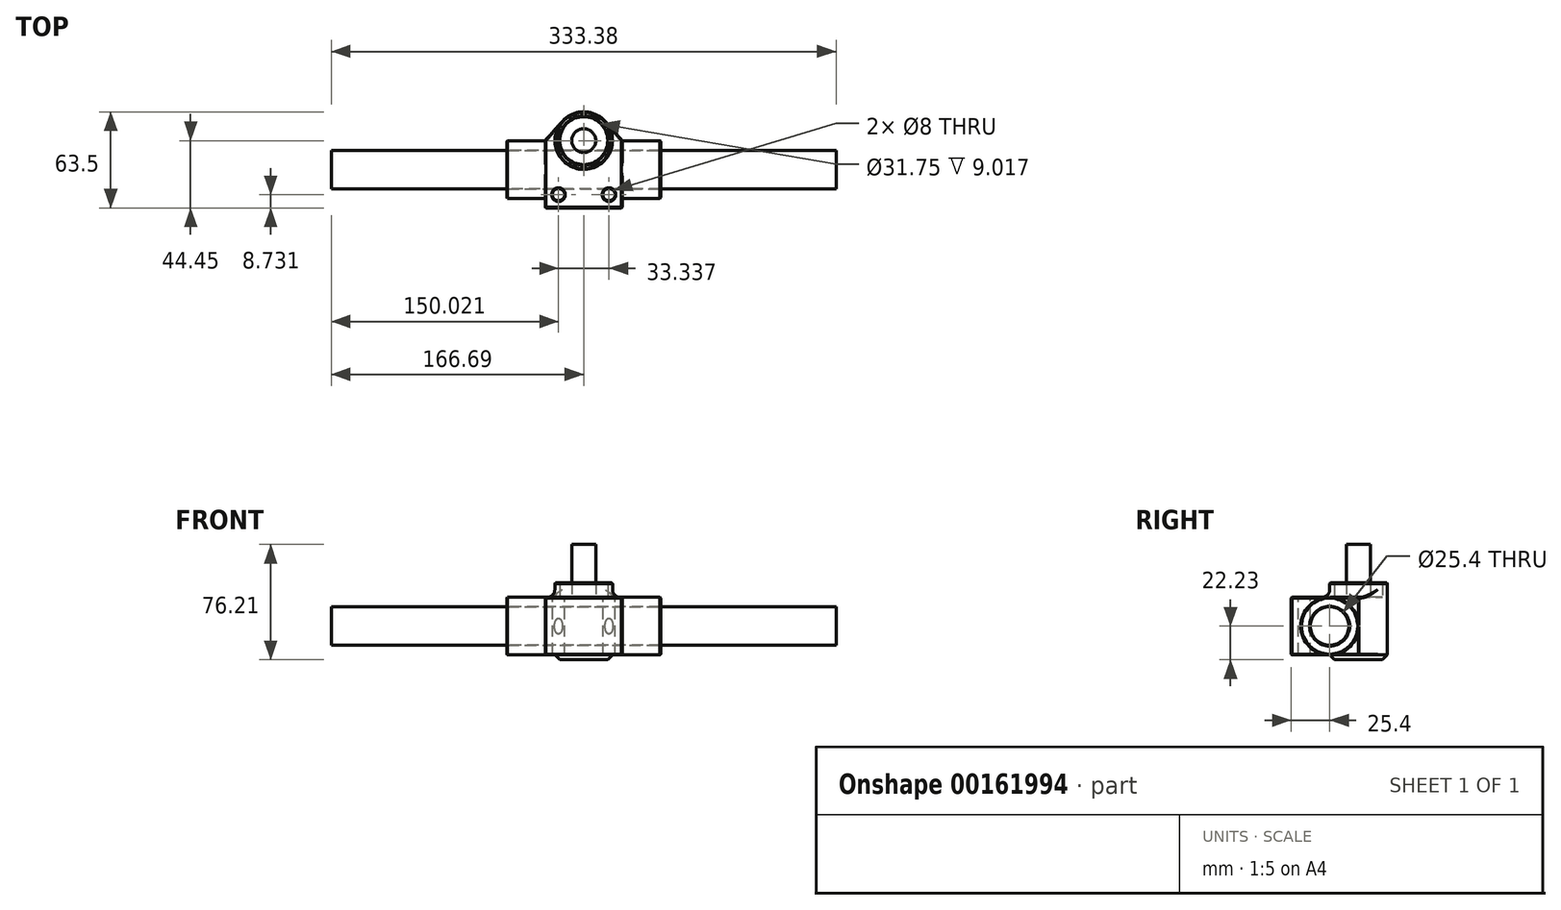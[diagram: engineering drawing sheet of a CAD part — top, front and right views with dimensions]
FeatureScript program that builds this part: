
annotation { "Feature Type Name" : "Feature", "Feature Type Description" : "" }
export const myFeature = defineFeature(function(context is Context, id is Id, definition is map)
    precondition{}
    {
        {
            var Q0;
            Q0=qCreatedBy(makeId("Top.planeOp"),FACE);
            var sketch = newSketch(context, id + "F0", { "sketchPlane" : qUnion([Q0])});
            skArc(sketch, "E0", {"start": v(-14.29, 12.6) * mm, "mid": v(0, 19.05) * mm, "end": v(14.29, 12.6) * mm});
            skLineSegment(sketch, "E1", {"start": v(-14.29, 12.6) * mm, "end": v(-25.4, 0) * mm});
            skLineSegment(sketch, "E2", {"start": v(14.29, 12.6) * mm, "end": v(25.4, 0) * mm});
            skLineSegment(sketch, "E3", {"start": v(25.4, 0) * mm, "end": v(25.4, -44.45) * mm});
            skLineSegment(sketch, "E4", {"start": v(25.4, -44.45) * mm, "end": v(-25.4, -44.45) * mm});
            skLineSegment(sketch, "E5", {"start": v(-25.4, -44.45) * mm, "end": v(-25.4, 0) * mm});
            skSolve(sketch);
        }
        {
            var Q0;
            Q0 = qSketchRegion(id + "F0", true);
            extrude(context, id + "F1", {"entities" : qUnion([Q0]), "endBound" : BoundingType.SYMMETRIC, "depth" : 38.1 * mm});
        }
        {
            var Q0;
            Q0=qCreatedBy(makeId("Right.planeOp"),FACE);
            var sketch = newSketch(context, id + "F2", { "sketchPlane" : qUnion([Q0])});
            skCircle(sketch, "E6", {"center": v(-19.05, 0) * mm, "radius": 19.05 * mm});
            skSolve(sketch);
        }
        {
            var Q0;
            Q0 = qSketchRegion(id + "F2", true);
            extrude(context, id + "F3", {"entities" : qUnion([Q0]), "operationType" : NewBodyOperationType.ADD, "endBound" : BoundingType.SYMMETRIC, "depth" : 101.6 * mm});
        }
        {
            var Q0;
            Q0=qCreatedBy(makeId("Right.planeOp"),FACE);
            var sketch = newSketch(context, id + "F4", { "sketchPlane" : qUnion([Q0])});
            skCircle(sketch, "E7", {"center": v(-19.05, 0) * mm, "radius": 12.7 * mm});
            skSolve(sketch);
        }
        {
            var Q0;
            Q0 = qSketchRegion(id + "F4", true);
            extrude(context, id + "F5", {"entities" : qUnion([Q0]), "operationType" : NewBodyOperationType.REMOVE, "endBound" : BoundingType.THROUGH_ALL, "oppositeDirection" : true, "depth" : 25.4 * mm, "hasSecondDirection" : true, "secondDirectionBound" : SecondDirectionBoundingType.THROUGH_ALL, "secondDirectionOppositeDirection" : false, "secondDirectionDepth" : 25.4 * mm});
        }
        {
            var Q0;
            Q0=makeQuery(id+"F1.opExtrude","CAP_FACE",FACE,{"disambiguationData":[OSD([sQuery(id+"F0.wireOp",EDGE,"E0"),sQuery(id+"F0.wireOp",EDGE,"E1"),sQuery(id+"F0.wireOp",EDGE,"E2"),sQuery(id+"F0.wireOp",EDGE,"E3"),sQuery(id+"F0.wireOp",EDGE,"E4"),sQuery(id+"F0.wireOp",EDGE,"E5")])],"isStart":false});
            var sketch = newSketch(context, id + "F6", { "sketchPlane" : qUnion([Q0])});
            skCircle(sketch, "E8", {"center": v(0, 0) * mm, "radius": 19.05 * mm});
            skCircle(sketch, "E9.0", {"center": v(0, 0) * mm, "radius": 15.88 * mm});
            skSolve(sketch);
        }
        {
            var Q0;
            Q0 = qSketchRegion(id + "F6", true);
            extrude(context, id + "F7", {"entities" : qUnion([Q0]), "operationType" : NewBodyOperationType.ADD, "depth" : 9.52 * mm});
        }
        {
            var Q0;
            Q0=makeQuery(id+"F7.boolean.opBoolean","SPLIT",FACE,{"disambiguationData":[TD([makeQuery(id+"F7.opExtrude","SWEPT_FACE",FACE,{"disambiguationData":[OSD([sQuery(id+"F6.wireOp",EDGE,"E9.0")])]})])],"derivedFrom":makeQuery(id+"F1.opExtrude","CAP_FACE",FACE,{"disambiguationData":[OSD([sQuery(id+"F0.wireOp",EDGE,"E0"),sQuery(id+"F0.wireOp",EDGE,"E1"),sQuery(id+"F0.wireOp",EDGE,"E2"),sQuery(id+"F0.wireOp",EDGE,"E3"),sQuery(id+"F0.wireOp",EDGE,"E4"),sQuery(id+"F0.wireOp",EDGE,"E5")])],"isStart":false})});
            var sketch = newSketch(context, id + "F8", { "sketchPlane" : qUnion([Q0])});
            skCircle(sketch, "E10", {"center": v(0, 0) * mm, "radius": 7.94 * mm});
            skSolve(sketch);
        }
        {
            var Q0;
            Q0=makeQuery(id+"F8.imprint","IMPRINT",FACE,{"disambiguationData":[TD([[makeQuery(id+"F8.imprint","IMPRINT",EDGE,{"derivedFrom":sQuery(id+"F8.wireOp",EDGE,"E10")}),1.0]])]});
            extrude(context, id + "F9", {"entities" : qUnion([Q0]), "depth" : 34.92 * mm});
        }
        {
            var Q0;
            Q0=makeQuery(id+"F1.opExtrude","CAP_FACE",FACE,{"disambiguationData":[OSD([sQuery(id+"F0.wireOp",EDGE,"E0"),sQuery(id+"F0.wireOp",EDGE,"E1"),sQuery(id+"F0.wireOp",EDGE,"E2"),sQuery(id+"F0.wireOp",EDGE,"E3"),sQuery(id+"F0.wireOp",EDGE,"E4"),sQuery(id+"F0.wireOp",EDGE,"E5")])],"isStart":true});
            var sketch = newSketch(context, id + "F10", { "sketchPlane" : qUnion([Q0])});
            skCircle(sketch, "E11", {"center": v(0, 0) * mm, "radius": 19.05 * mm});
            skSolve(sketch);
        }
        {
            var Q0;
            Q0 = qSketchRegion(id + "F10", true);
            extrude(context, id + "F11", {"entities" : qUnion([Q0]), "operationType" : NewBodyOperationType.ADD, "depth" : 3.17 * mm});
        }
        {
            var Q0;
            {var subQ0=sQuery(id+"F0.wireOp",EDGE,"E3");var subQ1=sQuery(id+"F0.wireOp",EDGE,"E2");var subQ2=sQuery(id+"F0.wireOp",EDGE,"E1");var subQ3=sQuery(id+"F0.wireOp",EDGE,"E0");var subQ4=sQuery(id+"F0.wireOp",EDGE,"E4");var subQ5=sQuery(id+"F0.wireOp",EDGE,"E5");Q0=makeQuery(id+"F7.boolean.opBoolean","SPLIT",FACE,{"disambiguationData":[TD([makeQuery(id+"F1.opExtrude","SWEPT_FACE",FACE,{"disambiguationData":[OSD([subQ3])]})])],"derivedFrom":makeQuery(id+"F1.opExtrude","CAP_FACE",FACE,{"disambiguationData":[OSD([subQ3,subQ2,subQ1,subQ0,subQ4,subQ5])],"isStart":false})});}
            var sketch = newSketch(context, id + "F12", { "sketchPlane" : qUnion([Q0])});
            skLineSegment(sketch, "E12", {"start": v(-16.67, -35.72) * mm, "end": v(16.67, -35.72) * mm, "construction": true});
            skPoint(sketch, "E13", {"position": v(0, -35.72) * mm});
            skCircle(sketch, "E14", {"center": v(-16.67, -35.72) * mm, "radius": 4 * mm});
            skCircle(sketch, "E15", {"center": v(16.67, -35.72) * mm, "radius": 4 * mm});
            skSolve(sketch);
        }
        {
            var Q0;
            Q0 = qSketchRegion(id + "F12", true);
            extrude(context, id + "F13", {"entities" : qUnion([Q0]), "operationType" : NewBodyOperationType.REMOVE, "endBound" : BoundingType.THROUGH_ALL, "oppositeDirection" : true, "depth" : 25.4 * mm});
        }
        {
            var Q0;
            Q0=makeQuery(id+"F11.opExtrude","CAP_EDGE",EDGE,{"disambiguationData":[OSD([sQuery(id+"F10.wireOp",EDGE,"E11")])],"isStart":false});
            chamfer(context, id + "F14", {"entities" : qUnion([Q0]), "width" : 3.17 * mm, "tangentPropagation" : true});
        }
        {
            var Q0;
            Q0=makeQuery(id+"F7.opExtrude","CAP_EDGE",EDGE,{"disambiguationData":[OSD([sQuery(id+"F6.wireOp",EDGE,"E8")])],"isStart":true});
            fillet(context, id + "F15", {"entities" : qUnion([Q0]), "radius" : 5.08 * mm, "tangentPropagation" : true, "allowEdgeOverflow" : false});
        }
        {
            var Q0;
            Q0=makeQuery(id+"F13.boolean.opBoolean","COPY",FACE,{"derivedFrom":makeQuery(id+"F13.opExtrude","SWEPT_FACE",FACE,{"disambiguationData":[OSD([sQuery(id+"F12.wireOp",EDGE,"E15")])]})});
            var Q1;
            Q1=makeQuery(id+"F13.boolean.opBoolean","COPY",FACE,{"derivedFrom":makeQuery(id+"F13.opExtrude","SWEPT_FACE",FACE,{"disambiguationData":[OSD([sQuery(id+"F12.wireOp",EDGE,"E14")])]})});
            var Q2;
            Q2=makeQuery(id+"F3.opExtrude","CAP_FACE",FACE,{"disambiguationData":[OSD([sQuery(id+"F2.wireOp",EDGE,"E6")])],"isStart":false});
            var Q3;
            Q3=makeQuery(id+"F7.opExtrude","CAP_FACE",FACE,{"disambiguationData":[OSD([sQuery(id+"F6.wireOp",EDGE,"E8"),sQuery(id+"F6.wireOp",EDGE,"E9.0")])],"isStart":false});
            var Q4;
            Q4=makeQuery(id+"F3.opExtrude","CAP_FACE",FACE,{"disambiguationData":[OSD([sQuery(id+"F2.wireOp",EDGE,"E6")])],"isStart":true});
            var Q5;
            {var subQ0=sQuery(id+"F0.wireOp",EDGE,"E3");var subQ1=sQuery(id+"F0.wireOp",EDGE,"E2");Q5=makeQuery(id+"F3.boolean.opBoolean","SPLIT",EDGE,{"disambiguationData":[TD([makeQuery(id+"F1.opExtrude","SWEPT_FACE",FACE,{"disambiguationData":[OSD([subQ1])]})])],"derivedFrom":makeQuery(id+"F1.opExtrude","CAP_EDGE",EDGE,{"disambiguationData":[OSD([subQ0])],"isStart":false})});}
            var Q6;
            Q6=makeQuery(id+"F1.opExtrude","CAP_EDGE",EDGE,{"disambiguationData":[OSD([sQuery(id+"F0.wireOp",EDGE,"E4")])],"isStart":false});
            var Q7;
            {var subQ0=sQuery(id+"F0.wireOp",EDGE,"E5");var subQ1=sQuery(id+"F0.wireOp",EDGE,"E4");Q7=makeQuery(id+"F3.boolean.opBoolean","SPLIT",EDGE,{"disambiguationData":[TD([makeQuery(id+"F1.opExtrude","SWEPT_FACE",FACE,{"disambiguationData":[OSD([subQ1])]})])],"derivedFrom":makeQuery(id+"F1.opExtrude","CAP_EDGE",EDGE,{"disambiguationData":[OSD([subQ0])],"isStart":false})});}
            var Q8;
            Q8=makeQuery(id+"F1.opExtrude","SWEPT_EDGE",EDGE,{"disambiguationData":[OSD([sQuery(id+"F0.wireOp",EDGE,"E4"),sQuery(id+"F0.wireOp",EDGE,"E5")])]});
            var Q9;
            Q9=makeQuery(id+"F1.opExtrude","SWEPT_EDGE",EDGE,{"disambiguationData":[OSD([sQuery(id+"F0.wireOp",EDGE,"E3"),sQuery(id+"F0.wireOp",EDGE,"E4")])]});
            var Q10;
            Q10=makeQuery(id+"F1.opExtrude","CAP_EDGE",EDGE,{"disambiguationData":[OSD([sQuery(id+"F0.wireOp",EDGE,"E4")])],"isStart":true});
            var Q11;
            {var subQ0=sQuery(id+"F0.wireOp",EDGE,"E4");var subQ1=sQuery(id+"F0.wireOp",EDGE,"E3");Q11=makeQuery(id+"F3.boolean.opBoolean","SPLIT",EDGE,{"disambiguationData":[TD([makeQuery(id+"F1.opExtrude","SWEPT_FACE",FACE,{"disambiguationData":[OSD([subQ0])]})])],"derivedFrom":makeQuery(id+"F1.opExtrude","CAP_EDGE",EDGE,{"disambiguationData":[OSD([subQ1])],"isStart":true})});}
            var Q12;
            {var subQ0=sQuery(id+"F0.wireOp",EDGE,"E5");var subQ1=sQuery(id+"F0.wireOp",EDGE,"E4");Q12=makeQuery(id+"F3.boolean.opBoolean","SPLIT",EDGE,{"disambiguationData":[TD([makeQuery(id+"F1.opExtrude","SWEPT_FACE",FACE,{"disambiguationData":[OSD([subQ1])]})])],"derivedFrom":makeQuery(id+"F1.opExtrude","CAP_EDGE",EDGE,{"disambiguationData":[OSD([subQ0])],"isStart":true})});}
            var Q13;
            Q13=makeQuery(id+"F1.opExtrude","CAP_EDGE",EDGE,{"disambiguationData":[OSD([sQuery(id+"F0.wireOp",EDGE,"E1")])],"isStart":true});
            var Q14;
            Q14=makeQuery(id+"F1.opExtrude","CAP_EDGE",EDGE,{"disambiguationData":[OSD([sQuery(id+"F0.wireOp",EDGE,"E2")])],"isStart":true});
            var Q15;
            {var subQ0=sQuery(id+"F0.wireOp",EDGE,"E5");var subQ1=sQuery(id+"F0.wireOp",EDGE,"E1");Q15=makeQuery(id+"F3.boolean.opBoolean","SPLIT",EDGE,{"disambiguationData":[TD([makeQuery(id+"F1.opExtrude","CAP_FACE",FACE,{"disambiguationData":[OSD([sQuery(id+"F0.wireOp",EDGE,"E0"),subQ1,sQuery(id+"F0.wireOp",EDGE,"E2"),sQuery(id+"F0.wireOp",EDGE,"E3"),sQuery(id+"F0.wireOp",EDGE,"E4"),subQ0])],"isStart":false})])],"derivedFrom":makeQuery(id+"F1.opExtrude","SWEPT_EDGE",EDGE,{"disambiguationData":[OSD([subQ1,subQ0])]})});}
            var Q16;
            {var subQ0=sQuery(id+"F0.wireOp",EDGE,"E3");var subQ1=sQuery(id+"F0.wireOp",EDGE,"E2");Q16=makeQuery(id+"F3.boolean.opBoolean","SPLIT",EDGE,{"disambiguationData":[TD([makeQuery(id+"F1.opExtrude","CAP_FACE",FACE,{"disambiguationData":[OSD([sQuery(id+"F0.wireOp",EDGE,"E0"),sQuery(id+"F0.wireOp",EDGE,"E1"),subQ1,subQ0,sQuery(id+"F0.wireOp",EDGE,"E4"),sQuery(id+"F0.wireOp",EDGE,"E5")])],"isStart":true})])],"derivedFrom":makeQuery(id+"F1.opExtrude","SWEPT_EDGE",EDGE,{"disambiguationData":[OSD([subQ1,subQ0])]})});}
            var Q17;
            Q17=makeQuery(id+"F15.opFillet","BLEND_EDGE",EDGE,{"blendedFrom":[makeQuery(id+"F7.opExtrude","CAP_EDGE",EDGE,{"disambiguationData":[OSD([sQuery(id+"F6.wireOp",EDGE,"E8")])],"isStart":true}),makeQuery(id+"F1.opExtrude","SWEPT_FACE",FACE,{"disambiguationData":[OSD([sQuery(id+"F0.wireOp",EDGE,"E2")])]})],"blendedInto":[makeQuery(id+"F1.opExtrude","SWEPT_FACE",FACE,{"disambiguationData":[OSD([sQuery(id+"F0.wireOp",EDGE,"E2")])]})]});
            var Q18;
            Q18=makeQuery(id+"F15.opFillet","BLEND_EDGE",EDGE,{"blendedFrom":[makeQuery(id+"F7.opExtrude","CAP_EDGE",EDGE,{"disambiguationData":[OSD([sQuery(id+"F6.wireOp",EDGE,"E8")])],"isStart":true}),makeQuery(id+"F1.opExtrude","SWEPT_FACE",FACE,{"disambiguationData":[OSD([sQuery(id+"F0.wireOp",EDGE,"E1")])]})],"blendedInto":[makeQuery(id+"F1.opExtrude","SWEPT_FACE",FACE,{"disambiguationData":[OSD([sQuery(id+"F0.wireOp",EDGE,"E1")])]})]});
            chamfer(context, id + "F16", {"entities" : qUnion([Q0, Q1, Q2, Q3, Q4, Q5, Q6, Q7, Q8, Q9, Q10, Q11, Q12, Q13, Q14, Q15, Q16, Q17, Q18]), "width" : 0.5 * mm, "tangentPropagation" : true});
        }
        {
            var Q0;
            Q0=qCreatedBy(makeId("Right.planeOp"),FACE);
            var sketch = newSketch(context, id + "F17", { "sketchPlane" : qUnion([Q0])});
            skCircle(sketch, "E16", {"center": v(-19.05, 0) * mm, "radius": 12.7 * mm});
            skSolve(sketch);
        }
        {
            var Q0;
            Q0 = qSketchRegion(id + "F17", true);
            extrude(context, id + "F18", {"entities" : qUnion([Q0]), "endBound" : BoundingType.SYMMETRIC, "depth" : 333.38 * mm});
        }
    });
